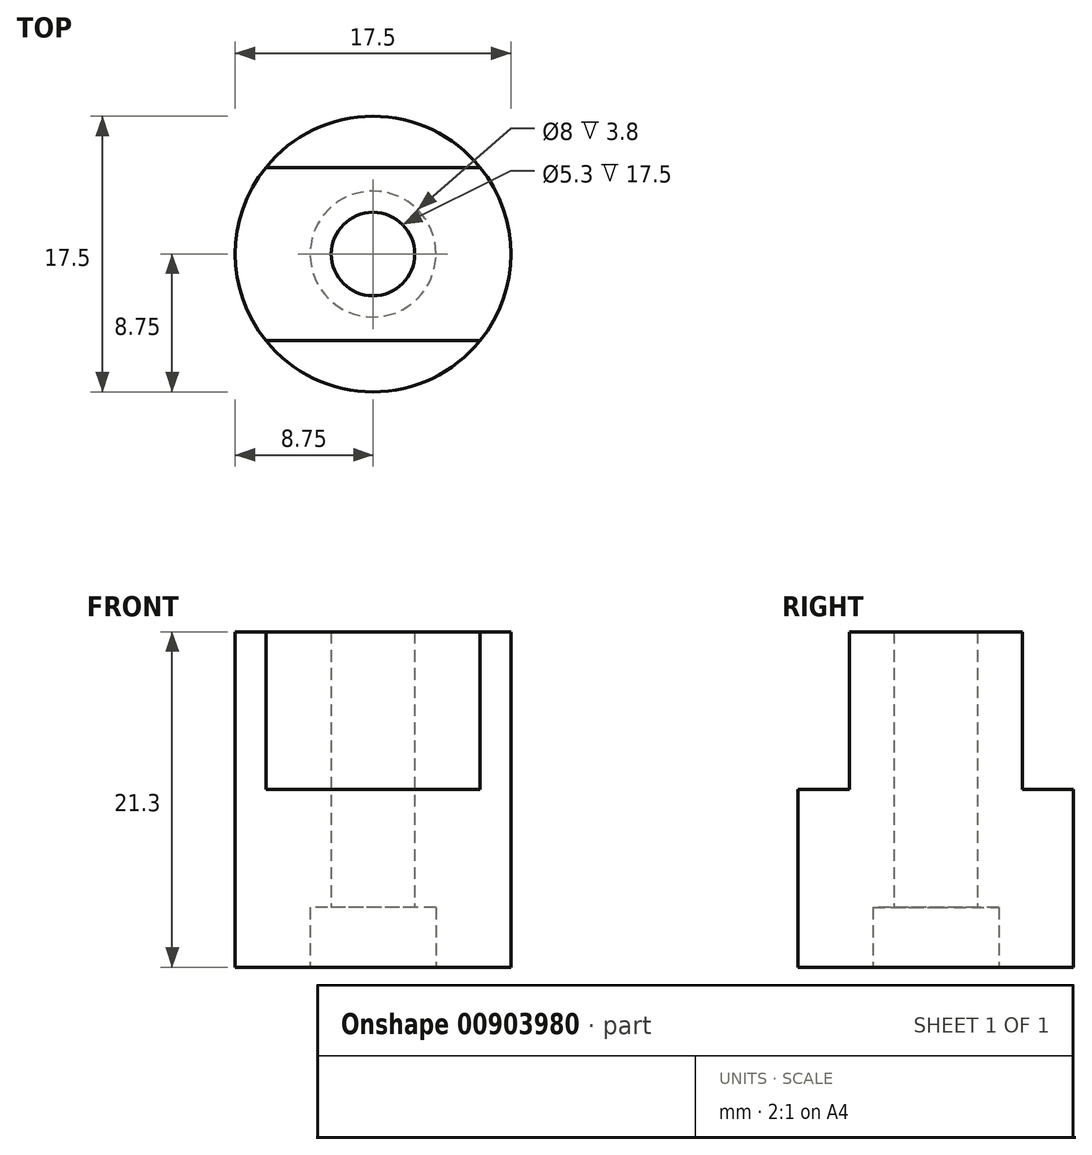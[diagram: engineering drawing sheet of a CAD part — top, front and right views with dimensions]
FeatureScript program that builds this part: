
annotation { "Feature Type Name" : "Feature", "Feature Type Description" : "" }
export const myFeature = defineFeature(function(context is Context, id is Id, definition is map)
    precondition{}
    {
        {
            var Q0;
            Q0=qCreatedBy(makeId("Top.planeOp"),FACE);
            var sketch = newSketch(context, id + "F0", { "sketchPlane" : qUnion([Q0])});
            skCircle(sketch, "E0", {"center": v(0, 0) * mm, "radius": 8.75 * mm});
            skCircle(sketch, "E1", {"center": v(0, 0) * mm, "radius": 2.65 * mm});
            skCircle(sketch, "E2", {"center": v(0, 0) * mm, "radius": 4 * mm});
            skSolve(sketch);
        }
        {
            var Q0;
            Q0=makeQuery(id+"F0.imprint","IMPRINT",FACE,{"disambiguationData":[TD([[makeQuery(id+"F0.imprint","IMPRINT",EDGE,{"derivedFrom":sQuery(id+"F0.wireOp",EDGE,"E0")}),1.0]])]});
            extrude(context, id + "F1", {"entities" : qUnion([Q0]), "depth" : (17.5 + 3.8) * mm, "offsetDistance" : 25 * mm});
        }
        {
            var Q0;
            Q0=makeQuery(id+"F0.imprint","IMPRINT",FACE,{"disambiguationData":[TD([[makeQuery(id+"F0.imprint","IMPRINT",EDGE,{"derivedFrom":sQuery(id+"F0.wireOp",EDGE,"E1")}),-1.0]])]});
            extrude(context, id + "F2", {"entities" : qUnion([Q0]), "operationType" : NewBodyOperationType.ADD, "depth" : (17.5 + 3.8) * mm, "offsetDistance" : 25 * mm, "hasSecondDirection" : true, "secondDirectionOppositeDirection" : false, "secondDirectionDepth" : 3.8 * mm});
        }
        {
            var Q0;
            {var subQ0=sQuery(id+"F0.wireOp",EDGE,"E2");Q0=makeQuery(id+"F2.boolean.opBoolean","MERGE",FACE,{"derivedFrom":[makeQuery(id+"F1.opExtrude","CAP_FACE",FACE,{"disambiguationData":[OSD([sQuery(id+"F0.wireOp",EDGE,"E0"),subQ0])],"isStart":false}),makeQuery(id+"F2.opExtrude","CAP_FACE",FACE,{"disambiguationData":[OSD([sQuery(id+"F0.wireOp",EDGE,"E1"),subQ0])],"isStart":false})]});}
            var sketch = newSketch(context, id + "F3", { "sketchPlane" : qUnion([Q0])});
            skLineSegment(sketch, "E3.bottom", {"start": v(12.5, 5.5) * mm, "end": v(-12.5, 5.5) * mm});
            skLineSegment(sketch, "E3.top", {"start": v(12.5, -5.5) * mm, "end": v(-12.5, -5.5) * mm});
            skLineSegment(sketch, "E3.left", {"start": v(12.5, 5.5) * mm, "end": v(12.5, -5.5) * mm});
            skLineSegment(sketch, "E3.right", {"start": v(-12.5, 5.5) * mm, "end": v(-12.5, -5.5) * mm});
            skPoint(sketch, "E3.middle", {"position": v(0, 0) * mm});
            skSolve(sketch);
        }
        {
            var Q0;
            {var subQ0=sQuery(id+"F3.wireOp",EDGE,"E3.top");var subQ1=makeQuery(id+"F1.opExtrude","CAP_EDGE",EDGE,{"disambiguationData":[OSD([sQuery(id+"F0.wireOp",EDGE,"E0")])],"isStart":false});var subQ2=makeQuery(id+"F3.imprint","INTERSECT",VERTEX,{"disambiguationData":[OD(0.0)],"derivedFrom":[subQ1,subQ0]});Q0=makeQuery(id+"F3.imprint","IMPRINT",FACE,{"disambiguationData":[TD([[makeQuery(id+"F3.imprint","IMPRINT",EDGE,{"disambiguationData":[TD([[subQ2,-1.0]])],"derivedFrom":subQ0}),1.0]])]});}
            var Q1;
            {var subQ0=sQuery(id+"F3.wireOp",EDGE,"E3.bottom");var subQ1=makeQuery(id+"F1.opExtrude","CAP_EDGE",EDGE,{"disambiguationData":[OSD([sQuery(id+"F0.wireOp",EDGE,"E0")])],"isStart":false});var subQ2=makeQuery(id+"F3.imprint","INTERSECT",VERTEX,{"disambiguationData":[OD(0.0)],"derivedFrom":[subQ1,subQ0]});Q1=makeQuery(id+"F3.imprint","IMPRINT",FACE,{"disambiguationData":[TD([[makeQuery(id+"F3.imprint","IMPRINT",EDGE,{"disambiguationData":[TD([[subQ2,-1.0]])],"derivedFrom":subQ0}),-1.0]])]});}
            extrude(context, id + "F4", {"entities" : qUnion([Q0, Q1]), "operationType" : NewBodyOperationType.REMOVE, "oppositeDirection" : true, "depth" : 10 * mm, "offsetDistance" : 25 * mm});
        }
    });
